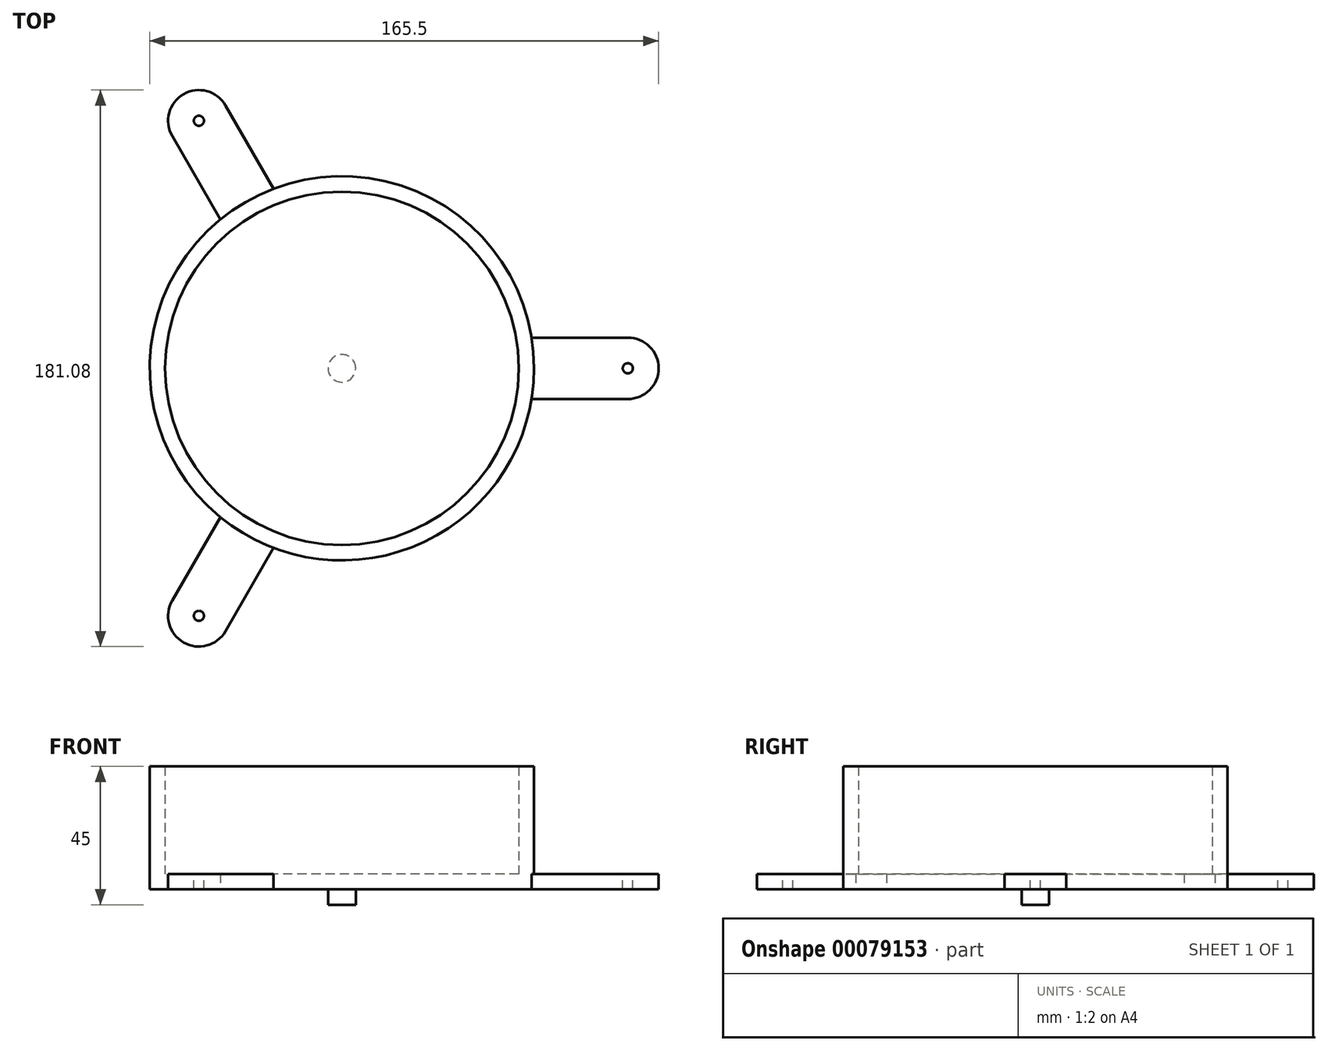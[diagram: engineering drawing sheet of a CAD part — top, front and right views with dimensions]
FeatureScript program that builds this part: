
annotation { "Feature Type Name" : "Feature", "Feature Type Description" : "" }
export const myFeature = defineFeature(function(context is Context, id is Id, definition is map)
    precondition{}
    {
        {
            assignVariable(context, id + "F0", {"name" : "tray_thickness", "anyValue" : 5 * mm});
        }
        {
            assignVariable(context, id + "F1", {"name" : "tray_height", "anyValue" : 35 * mm});
        }
        {
            var Q0;
            Q0=qCreatedBy(makeId("Top.planeOp"),FACE);
            var sketch = newSketch(context, id + "F2", { "sketchPlane" : qUnion([Q0])});
            skCircle(sketch, "E0", {"center": v(0, 0) * mm, "radius": 62.5 * mm});
            skLineSegment(sketch, "E1", {"start": v(61.7, 10) * mm, "end": v(93, 10) * mm});
            skLineSegment(sketch, "E2", {"start": v(93, -10) * mm, "end": v(61.7, -10) * mm});
            skArc(sketch, "E3", {"start": v(93, -10) * mm, "mid": v(103, 0) * mm, "end": v(93, 10) * mm});
            skLineSegment(sketch, "E4.1.0", {"start": v(-39.5, 48.43) * mm, "end": v(-55.16, 75.54) * mm});
            skArc(sketch, "E4.1.1", {"start": v(-37.84, 85.54) * mm, "mid": v(-51.5, 89.2) * mm, "end": v(-55.16, 75.54) * mm});
            skLineSegment(sketch, "E4.1.2", {"start": v(-37.84, 85.54) * mm, "end": v(-22.19, 58.43) * mm});
            skLineSegment(sketch, "E4.2.0", {"start": v(-22.19, -58.43) * mm, "end": v(-37.84, -85.54) * mm});
            skArc(sketch, "E4.2.1", {"start": v(-55.16, -75.54) * mm, "mid": v(-51.5, -89.2) * mm, "end": v(-37.84, -85.54) * mm});
            skLineSegment(sketch, "E4.2.2", {"start": v(-55.16, -75.54) * mm, "end": v(-39.5, -48.43) * mm});
            skSolve(sketch);
        }
        {
            var Q0;
            {var subQ0=sQuery(id+"F2.wireOp",EDGE,"E4.1.0");Q0=makeQuery(id+"F2.imprint","IMPRINT",FACE,{"disambiguationData":[TD([[makeQuery(id+"F2.imprint","IMPRINT",EDGE,{"derivedFrom":subQ0}),-1.0]])]});}
            var Q1;
            {var subQ0=sQuery(id+"F2.wireOp",EDGE,"E0");var subQ5=makeQuery(id+"F2.imprint","INTERSECT",VERTEX,{"derivedFrom":[subQ0,sQuery(id+"F2.wireOp",EDGE,"E1")]});Q1=makeQuery(id+"F2.imprint","IMPRINT",FACE,{"disambiguationData":[TD([[makeQuery(id+"F2.imprint","IMPRINT",EDGE,{"disambiguationData":[TD([[subQ5,-1.0]])],"derivedFrom":subQ0}),1.0]])]});}
            var Q2;
            {var subQ0=sQuery(id+"F2.wireOp",EDGE,"E1");Q2=makeQuery(id+"F2.imprint","IMPRINT",FACE,{"disambiguationData":[TD([[makeQuery(id+"F2.imprint","IMPRINT",EDGE,{"derivedFrom":subQ0}),-1.0]])]});}
            var Q3;
            {var subQ0=sQuery(id+"F2.wireOp",EDGE,"E4.2.0");Q3=makeQuery(id+"F2.imprint","IMPRINT",FACE,{"disambiguationData":[TD([[makeQuery(id+"F2.imprint","IMPRINT",EDGE,{"derivedFrom":subQ0}),-1.0]])]});}
            extrude(context, id + "F3", {"entities" : qUnion([Q0, Q1, Q2, Q3]), "depth" : (getVariable(context, 'tray_thickness'))});
        }
        {
            var Q0;
            Q0=makeQuery(id+"F3.opExtrude","CAP_FACE",FACE,{"disambiguationData":[OSD([sQuery(id+"F2.wireOp",EDGE,"E0"),sQuery(id+"F2.wireOp",EDGE,"E1"),sQuery(id+"F2.wireOp",EDGE,"E2"),sQuery(id+"F2.wireOp",EDGE,"E3"),sQuery(id+"F2.wireOp",EDGE,"E4.1.0"),sQuery(id+"F2.wireOp",EDGE,"E4.1.1"),sQuery(id+"F2.wireOp",EDGE,"E4.1.2"),sQuery(id+"F2.wireOp",EDGE,"E4.2.0"),sQuery(id+"F2.wireOp",EDGE,"E4.2.1"),sQuery(id+"F2.wireOp",EDGE,"E4.2.2")])],"isStart":false});
            var sketch = newSketch(context, id + "F4", { "sketchPlane" : qUnion([Q0])});
            skPoint(sketch, "E5", {"position": v(93, 0) * mm});
            skPoint(sketch, "E6.1.0", {"position": v(-46.5, 80.54) * mm});
            skPoint(sketch, "E6.2.0", {"position": v(-46.5, -80.54) * mm});
            skPoint(sketch, "E6.center", {"position": v(0, 0) * mm});
            skSolve(sketch);
        }
        {
            var Q0;
            Q0=sQuery(id+"F4.wireOp",VERTEX,"E6.1.0");
            var Q1;
            Q1=sQuery(id+"F4.wireOp",VERTEX,"E5");
            var Q2;
            Q2=sQuery(id+"F4.wireOp",VERTEX,"E6.2.0");
            var Q3;
            Q3=makeQuery(id+"F3.opExtrude","SWEPT_BODY",BODY,{"disambiguationData":[OSD([sQuery(id+"F2.wireOp",EDGE,"E0"),sQuery(id+"F2.wireOp",EDGE,"E1"),sQuery(id+"F2.wireOp",EDGE,"E2"),sQuery(id+"F2.wireOp",EDGE,"E3"),sQuery(id+"F2.wireOp",EDGE,"E4.1.0"),sQuery(id+"F2.wireOp",EDGE,"E4.1.1"),sQuery(id+"F2.wireOp",EDGE,"E4.1.2"),sQuery(id+"F2.wireOp",EDGE,"E4.2.0"),sQuery(id+"F2.wireOp",EDGE,"E4.2.1"),sQuery(id+"F2.wireOp",EDGE,"E4.2.2")])]});
            hole(context, id + "F5", {"style" : HoleStyle.SIMPLE, "endStyle" : HoleEndStyle.THROUGH, "standardTappedOrClearance" : lookupTablePath({ "standard" : "ISO", "engagement" : "75%", "pitch" : "0.7 mm", "size" : "M4", "type" : "Tapped" }), "standardBlindInLast" : lookupTablePath({ "standard" : "ISO", "engagement" : "75%", "pitch" : "0.7 mm", "size" : "M4", "type" : "Tapped" }), "holeDiameter" : 3.3 * mm, "locations" : qUnion([Q0, Q1, Q2]), "scope" : qUnion([Q3]), "isTappedThrough" : true, "majorDiameter" : 4 * mm, "showTappedDepth" : true});
        }
        {
            var Q0;
            Q0=makeQuery(id+"F3.opExtrude","CAP_FACE",FACE,{"disambiguationData":[OSD([sQuery(id+"F2.wireOp",EDGE,"E0"),sQuery(id+"F2.wireOp",EDGE,"E1"),sQuery(id+"F2.wireOp",EDGE,"E2"),sQuery(id+"F2.wireOp",EDGE,"E3"),sQuery(id+"F2.wireOp",EDGE,"E4.1.0"),sQuery(id+"F2.wireOp",EDGE,"E4.1.1"),sQuery(id+"F2.wireOp",EDGE,"E4.1.2"),sQuery(id+"F2.wireOp",EDGE,"E4.2.0"),sQuery(id+"F2.wireOp",EDGE,"E4.2.1"),sQuery(id+"F2.wireOp",EDGE,"E4.2.2")])],"isStart":true});
            var sketch = newSketch(context, id + "F6", { "sketchPlane" : qUnion([Q0])});
            skCircle(sketch, "E7", {"center": v(0, 0) * mm, "radius": 4.5 * mm});
            skSolve(sketch);
        }
        {
            var Q0;
            Q0 = qSketchRegion(id + "F6", true);
            extrude(context, id + "F7", {"entities" : qUnion([Q0]), "operationType" : NewBodyOperationType.ADD, "depth" : getVariable(context, 'tray_thickness')});
        }
        {
            var Q0;
            Q0=makeQuery(id+"F3.opExtrude","CAP_FACE",FACE,{"disambiguationData":[OSD([sQuery(id+"F2.wireOp",EDGE,"E0"),sQuery(id+"F2.wireOp",EDGE,"E1"),sQuery(id+"F2.wireOp",EDGE,"E2"),sQuery(id+"F2.wireOp",EDGE,"E3"),sQuery(id+"F2.wireOp",EDGE,"E4.1.0"),sQuery(id+"F2.wireOp",EDGE,"E4.1.1"),sQuery(id+"F2.wireOp",EDGE,"E4.1.2"),sQuery(id+"F2.wireOp",EDGE,"E4.2.0"),sQuery(id+"F2.wireOp",EDGE,"E4.2.1"),sQuery(id+"F2.wireOp",EDGE,"E4.2.2")])],"isStart":false});
            var sketch = newSketch(context, id + "F8", { "sketchPlane" : qUnion([Q0])});
            skCircle(sketch, "E8", {"center": v(0, 0) * mm, "radius": 62.5 * mm});
            skCircle(sketch, "E9", {"center": v(0, 0) * mm, "radius": 57.5 * mm});
            skSolve(sketch);
        }
        {
            var Q0;
            Q0=makeQuery(id+"F8.imprint","IMPRINT",FACE,{"disambiguationData":[TD([[makeQuery(id+"F8.imprint","IMPRINT",EDGE,{"derivedFrom":sQuery(id+"F8.wireOp",EDGE,"E9")}),-1.0]])]});
            extrude(context, id + "F9", {"entities" : qUnion([Q0]), "operationType" : NewBodyOperationType.ADD, "depth" : getVariable(context, 'tray_height')});
        }
    });
